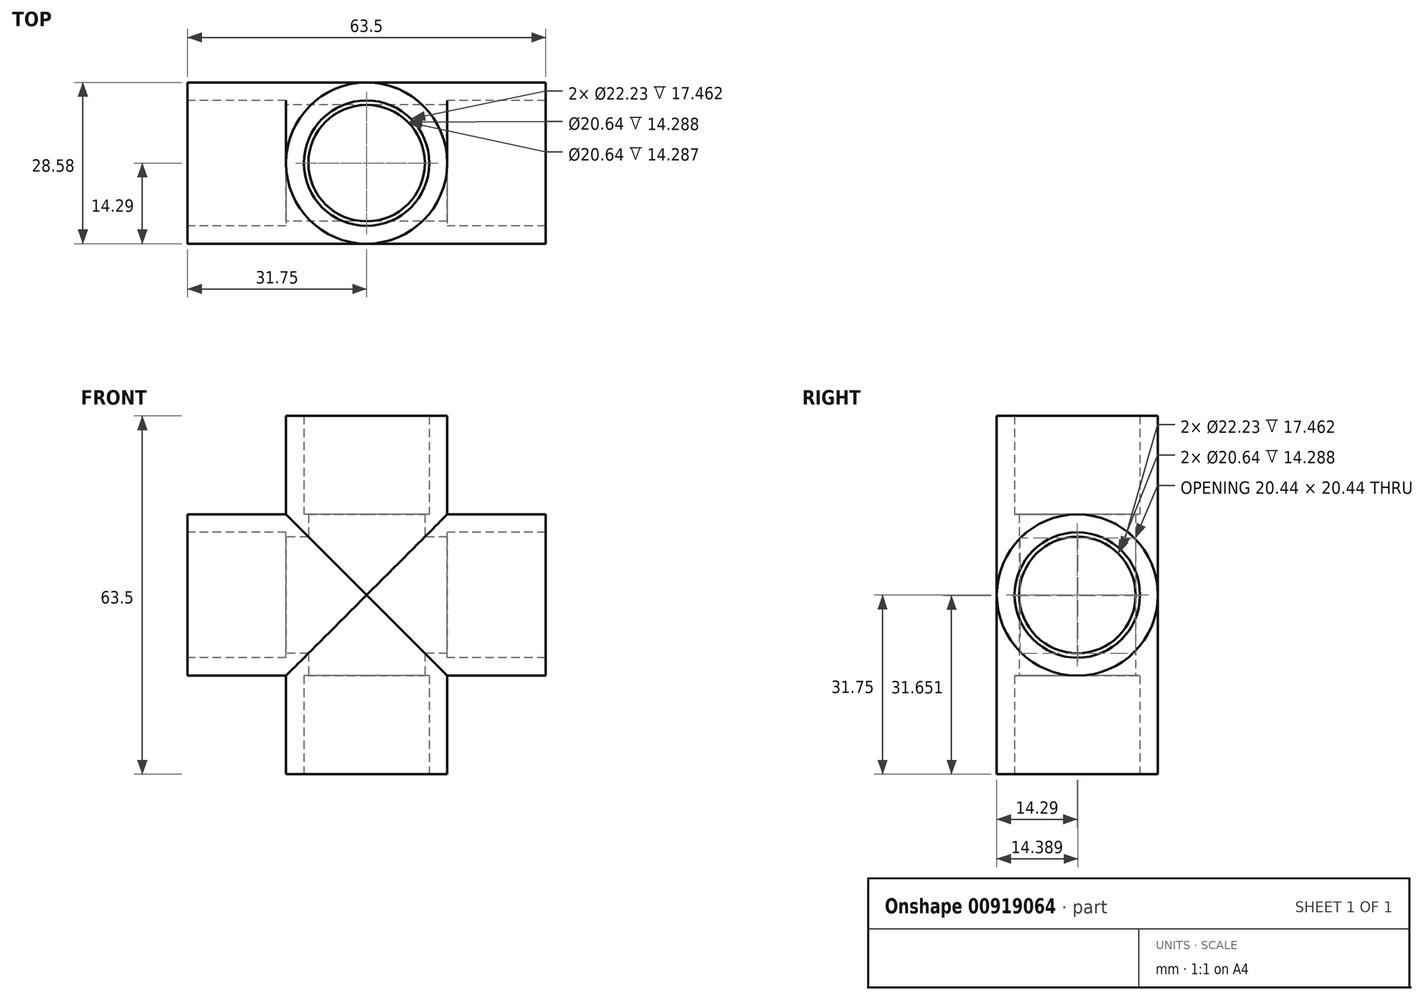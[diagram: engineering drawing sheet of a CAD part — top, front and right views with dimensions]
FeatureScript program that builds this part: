
annotation { "Feature Type Name" : "Feature", "Feature Type Description" : "" }
export const myFeature = defineFeature(function(context is Context, id is Id, definition is map)
    precondition{}
    {
        {
            var Q0;
            Q0=qCreatedBy(makeId("Top.planeOp"),FACE);
            var sketch = newSketch(context, id + "F0", { "sketchPlane" : qUnion([Q0])});
            skCircle(sketch, "E0", {"center": v(0, 0) * mm, "radius": 14.29 * mm});
            skCircle(sketch, "E1", {"center": v(0, 0) * mm, "radius": 11.11 * mm});
            skCircle(sketch, "E2", {"center": v(0, 0) * mm, "radius": 10.32 * mm});
            skSolve(sketch);
        }
        {
            var Q0;
            Q0 = qSketchRegion(id + "F0", true);
            extrude(context, id + "F1", {"entities" : qUnion([Q0]), "endBound" : BoundingType.SYMMETRIC, "depth" : 63.5 * mm, "offsetDistance" : 25.4 * mm});
        }
        {
            var Q0;
            Q0=makeQuery(id+"F0.imprint","IMPRINT",FACE,{"disambiguationData":[TD([[makeQuery(id+"F0.imprint","IMPRINT",EDGE,{"derivedFrom":sQuery(id+"F0.wireOp",EDGE,"E1")}),1.0]])]});
            extrude(context, id + "F2", {"entities" : qUnion([Q0]), "operationType" : NewBodyOperationType.ADD, "endBound" : BoundingType.SYMMETRIC, "depth" : 28.57 * mm, "offsetDistance" : 25.4 * mm});
        }
        {
            var Q0;
            Q0=qCreatedBy(makeId("Right.planeOp"),FACE);
            var sketch = newSketch(context, id + "F3", { "sketchPlane" : qUnion([Q0])});
            skCircle(sketch, "E3", {"center": v(0, 0) * mm, "radius": 14.29 * mm});
            skCircle(sketch, "E4", {"center": v(0, 0) * mm, "radius": 11.11 * mm});
            skCircle(sketch, "E5", {"center": v(0, 0) * mm, "radius": 10.32 * mm});
            skSolve(sketch);
        }
        {
            var Q0;
            Q0=makeQuery(id+"F3.imprint","IMPRINT",FACE,{"disambiguationData":[TD([[makeQuery(id+"F3.imprint","IMPRINT",EDGE,{"derivedFrom":sQuery(id+"F3.wireOp",EDGE,"E3")}),1.0]])]});
            var Q1;
            Q1=sQuery(id+"F3.wireOp",EDGE,"E3");
            var Q2;
            Q2=sQuery(id+"F3.wireOp",EDGE,"E4");
            var Q3;
            Q3=sQuery(id+"F3.wireOp",EDGE,"E5");
            extrude(context, id + "F4", {"entities" : qUnion([Q0]), "operationType" : NewBodyOperationType.ADD, "surfaceEntities" : qUnion([Q1, Q2, Q3]), "endBound" : BoundingType.SYMMETRIC, "depth" : 63.5 * mm, "offsetDistance" : 25.4 * mm});
        }
        {
            var Q0;
            Q0=makeQuery(id+"F3.imprint","IMPRINT",FACE,{"disambiguationData":[TD([[makeQuery(id+"F3.imprint","IMPRINT",EDGE,{"derivedFrom":sQuery(id+"F3.wireOp",EDGE,"E4")}),1.0]])]});
            extrude(context, id + "F5", {"entities" : qUnion([Q0]), "operationType" : NewBodyOperationType.ADD, "endBound" : BoundingType.SYMMETRIC, "depth" : 28.57 * mm, "offsetDistance" : 25.4 * mm});
        }
        {
            var Q0;
            Q0=makeQuery(id+"F0.imprint","IMPRINT",FACE,{"disambiguationData":[TD([[makeQuery(id+"F0.imprint","IMPRINT",EDGE,{"derivedFrom":sQuery(id+"F0.wireOp",EDGE,"E2")}),1.0]])]});
            extrude(context, id + "F6", {"entities" : qUnion([Q0]), "operationType" : NewBodyOperationType.REMOVE, "endBound" : BoundingType.SYMMETRIC, "oppositeDirection" : true, "depth" : 28.57 * mm, "offsetDistance" : 25.4 * mm});
        }
        {
            var Q0;
            Q0=makeQuery(id+"F3.imprint","IMPRINT",FACE,{"disambiguationData":[TD([[makeQuery(id+"F3.imprint","IMPRINT",EDGE,{"derivedFrom":sQuery(id+"F3.wireOp",EDGE,"E5")}),1.0]])]});
            extrude(context, id + "F7", {"entities" : qUnion([Q0]), "operationType" : NewBodyOperationType.REMOVE, "endBound" : BoundingType.SYMMETRIC, "depth" : 28.57 * mm, "offsetDistance" : 25.4 * mm});
        }
    });
